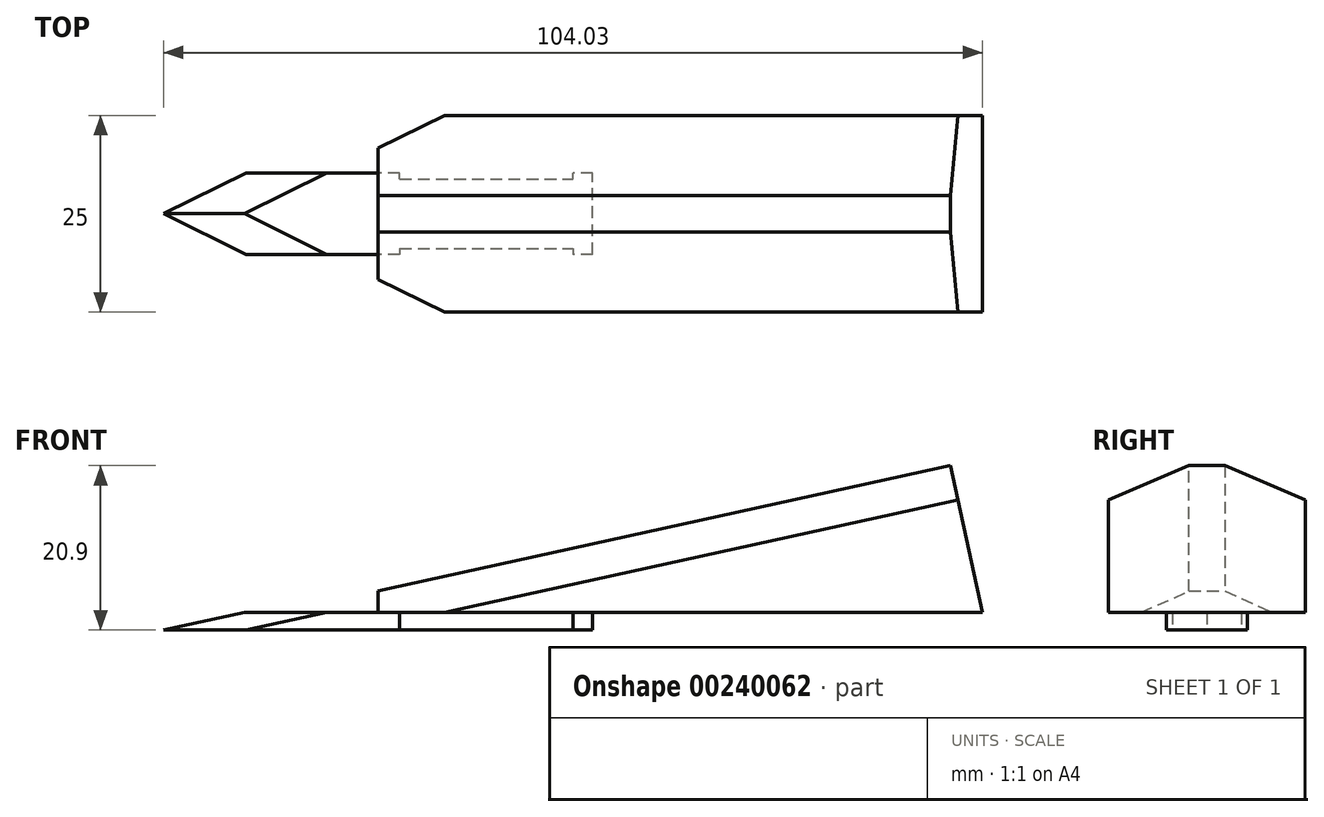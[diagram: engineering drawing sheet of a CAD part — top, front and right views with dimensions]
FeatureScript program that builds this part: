
annotation { "Feature Type Name" : "Feature", "Feature Type Description" : "" }
export const myFeature = defineFeature(function(context is Context, id is Id, definition is map)
    precondition{}
    {
        {
            var Q0;
            Q0=qCreatedBy(makeId("Top.planeOp"),FACE);
            var sketch = newSketch(context, id + "F0", { "sketchPlane" : qUnion([Q0])});
            skLineSegment(sketch, "E0.bottom", {"start": v(40.28, -18.54) * mm, "end": v(-40.28, -18.54) * mm});
            skLineSegment(sketch, "E0.top", {"start": v(40.28, 18.54) * mm, "end": v(-40.28, 18.54) * mm});
            skLineSegment(sketch, "E0.left", {"start": v(40.28, -18.54) * mm, "end": v(40.28, 18.54) * mm});
            skLineSegment(sketch, "E0.right", {"start": v(-40.28, -18.54) * mm, "end": v(-40.28, 18.54) * mm});
            skPoint(sketch, "E0.middle", {"position": v(0, 0) * mm});
            skLineSegment(sketch, "E1.bottom", {"start": v(27.25, -5.15) * mm, "end": v(-27.25, -5.15) * mm});
            skLineSegment(sketch, "E1.top", {"start": v(27.25, 5.15) * mm, "end": v(-27.25, 5.15) * mm});
            skLineSegment(sketch, "E1.left", {"start": v(27.25, -5.15) * mm, "end": v(27.25, 5.15) * mm});
            skLineSegment(sketch, "E1.right", {"start": v(-27.25, -5.15) * mm, "end": v(-27.25, 5.15) * mm});
            skLineSegment(sketch, "E2.bottom", {"start": v(2.75, -4.4) * mm, "end": v(24.75, -4.4) * mm});
            skLineSegment(sketch, "E2.top", {"start": v(2.75, -5.15) * mm, "end": v(24.75, -5.15) * mm});
            skLineSegment(sketch, "E2.left", {"start": v(2.75, -4.4) * mm, "end": v(2.75, -5.15) * mm});
            skLineSegment(sketch, "E2.right", {"start": v(24.75, -4.4) * mm, "end": v(24.75, -5.15) * mm});
            skLineSegment(sketch, "E3.MirrorCS", {"start": v(24.75, 4.4) * mm, "end": v(24.75, 5.15) * mm});
            skLineSegment(sketch, "E4.MirrorCS", {"start": v(2.75, 4.4) * mm, "end": v(24.75, 4.4) * mm});
            skLineSegment(sketch, "E5.MirrorCS", {"start": v(2.75, 4.4) * mm, "end": v(2.75, 5.15) * mm});
            skSolve(sketch);
        }
        {
            var Q0;
            {var subQ5=sQuery(id+"F0.wireOp",EDGE,"E1.left");Q0=makeQuery(id+"F0.imprint","IMPRINT",FACE,{"disambiguationData":[TD([[makeQuery(id+"F0.imprint","IMPRINT",EDGE,{"derivedFrom":subQ5}),1.0]])]});}
            extrude(context, id + "F1", {"entities" : qUnion([Q0]), "depth" : 2.25 * mm});
        }
        {
            var Q0;
            Q0=qCreatedBy(makeId("Front.planeOp"),FACE);
            var sketch = newSketch(context, id + "F2", { "sketchPlane" : qUnion([Q0])});
            skPoint(sketch, "E6.0", {"position": v(-27.25, 0) * mm});
            skLineSegment(sketch, "E7.0", {"start": v(2.75, 2.25) * mm, "end": v(-27.25, 2.25) * mm});
            skLineSegment(sketch, "E8.0", {"start": v(2.75, 0) * mm, "end": v(-27.25, 0) * mm});
            skLineSegment(sketch, "E9", {"start": v(-27.25, 0) * mm, "end": v(-17, 2.25) * mm});
            skLineSegment(sketch, "E10", {"start": v(-27.25, 0) * mm, "end": v(-6.52, 2.25) * mm, "construction": true});
            skLineSegment(sketch, "E11", {"start": v(-6.52, 2.25) * mm, "end": v(-16.78, 0) * mm});
            skLineSegment(sketch, "E12", {"start": v(-27.25, 0) * mm, "end": v(-27.25, 2.25) * mm});
            skPoint(sketch, "E13", {"position": v(-17, 2.25) * mm});
            skSolve(sketch);
        }
        {
            var Q0;
            {var subQ2=sQuery(id+"F2.wireOp",EDGE,"E9");Q0=makeQuery(id+"F2.imprint","IMPRINT",FACE,{"disambiguationData":[TD([[makeQuery(id+"F2.imprint","IMPRINT",EDGE,{"derivedFrom":subQ2}),1.0]])]});}
            extrude(context, id + "F3", {"entities" : qUnion([Q0]), "operationType" : NewBodyOperationType.REMOVE, "endBound" : BoundingType.SYMMETRIC, "oppositeDirection" : true, "depth" : 25 * mm});
        }
        {
            var Q0;
            {var subQ0=sQuery(id+"F0.wireOp",EDGE,"E1.bottom");Q0=makeQuery(id+"F1.opExtrude","SWEPT_FACE",FACE,{"disambiguationData":[OSD([subQ0]),TDD([makeQuery(id+"F0.imprint","IMPRINT",EDGE,{"disambiguationData":[TD([[makeQuery(id+"F0.imprint","INTERSECT",VERTEX,{"derivedFrom":[subQ0,sQuery(id+"F0.wireOp",EDGE,"E1.right")]}),1.0]])],"derivedFrom":subQ0})])]});}
            var sketch = newSketch(context, id + "F4", { "sketchPlane" : qUnion([Q0])});
            skLineSegment(sketch, "E14.0", {"start": v(-6.52, 2.25) * mm, "end": v(-16.78, 0) * mm});
            skLineSegment(sketch, "E15.0", {"start": v(2.75, 0) * mm, "end": v(-27.25, 0) * mm});
            skLineSegment(sketch, "E16.0", {"start": v(2.75, 2.25) * mm, "end": v(-27.25, 2.25) * mm});
            skPoint(sketch, "E17", {"position": v(-6.52, 2.25) * mm});
            skPoint(sketch, "E18", {"position": v(-16.78, 0) * mm});
            skSolve(sketch);
        }
        {
            var Q0;
            Q0=sQuery(id+"F2.wireOp",VERTEX,"E6.0");
            var Q1;
            Q1=sQuery(id+"F2.wireOp",VERTEX,"E13");
            var Q2;
            Q2=sQuery(id+"F4.wireOp",VERTEX,"E17");
            cPlane(context, id + "F5", {"entities" : qUnion([Q0, Q1, Q2]), "cplaneType" : CPlaneType.THREE_POINT, "offset" : 25 * mm, "width" : 150 * mm, "height" : 150 * mm});
        }
        {
            var Q0;
            Q0=qCreatedBy(id+"F5.planeOp",FACE);
            var sketch = newSketch(context, id + "F6", { "sketchPlane" : qUnion([Q0])});
            skPoint(sketch, "E19.0", {"position": v(-26.72, 0) * mm});
            skPoint(sketch, "E20.0", {"position": v(-16.26, 0.92) * mm});
            skPoint(sketch, "E21.0", {"position": v(-5.58, -3.79) * mm});
            skPoint(sketch, "E22.0", {"position": v(-16.04, -4.7) * mm});
            skLineSegment(sketch, "E23", {"start": v(-26.72, 0) * mm, "end": v(-16.26, 0.92) * mm});
            skLineSegment(sketch, "E24", {"start": v(-5.58, -3.79) * mm, "end": v(-16.26, 0.92) * mm});
            skLineSegment(sketch, "E25", {"start": v(-16.04, -4.7) * mm, "end": v(-26.72, 0) * mm});
            skLineSegment(sketch, "E26", {"start": v(-16.04, -4.7) * mm, "end": v(-5.58, -3.79) * mm});
            skLineSegment(sketch, "E27", {"start": v(-16.26, 0.92) * mm, "end": v(-27.12, 5.7) * mm});
            skLineSegment(sketch, "E28", {"start": v(-26.72, 0) * mm, "end": v(-37.58, 4.78) * mm});
            skLineSegment(sketch, "E29", {"start": v(-27.12, 5.7) * mm, "end": v(-37.58, 4.78) * mm});
            skLineSegment(sketch, "E30", {"start": v(-16.04, -4.7) * mm, "end": v(-43.24, -7.09) * mm});
            skLineSegment(sketch, "E31", {"start": v(-43.24, -7.09) * mm, "end": v(-37.58, 4.78) * mm});
            skSolve(sketch);
        }
        {
            var Q0;
            Q0=makeQuery(id+"F6.imprint","IMPRINT",FACE,{"disambiguationData":[TD([[makeQuery(id+"F6.imprint","IMPRINT",EDGE,{"derivedFrom":sQuery(id+"F6.wireOp",EDGE,"E23")}),-1.0]])]});
            var Q1;
            Q1=makeQuery(id+"F6.imprint","IMPRINT",FACE,{"disambiguationData":[TD([[makeQuery(id+"F6.imprint","IMPRINT",EDGE,{"derivedFrom":sQuery(id+"F6.wireOp",EDGE,"E23")}),1.0]])]});
            var Q2;
            Q2=makeQuery(id+"F6.imprint","IMPRINT",FACE,{"disambiguationData":[TD([[makeQuery(id+"F6.imprint","IMPRINT",EDGE,{"derivedFrom":sQuery(id+"F6.wireOp",EDGE,"E25")}),1.0]])]});
            extrude(context, id + "F7", {"entities" : qUnion([Q0, Q1, Q2]), "depth" : 25 * mm});
        }
        {
            var Q0;
            Q0=makeQuery(id+"F7.opExtrude","SWEPT_BODY",BODY,{"disambiguationData":[OSD([sQuery(id+"F6.wireOp",EDGE,"E24"),sQuery(id+"F6.wireOp",EDGE,"E26"),sQuery(id+"F6.wireOp",EDGE,"E27"),sQuery(id+"F6.wireOp",EDGE,"E29"),sQuery(id+"F6.wireOp",EDGE,"E30"),sQuery(id+"F6.wireOp",EDGE,"E31")])]});
            var Q1;
            Q1=qCreatedBy(makeId("Front.planeOp"),FACE);
            mirror(context, id + "F8", {"entities" : qUnion([Q0]), "mirrorPlane" : qUnion([Q1])});
        }
        {
            var Q0;
            Q0=makeQuery(id+"F7.opExtrude","SWEPT_BODY",BODY,{"disambiguationData":[OSD([sQuery(id+"F6.wireOp",EDGE,"E24"),sQuery(id+"F6.wireOp",EDGE,"E26"),sQuery(id+"F6.wireOp",EDGE,"E27"),sQuery(id+"F6.wireOp",EDGE,"E29"),sQuery(id+"F6.wireOp",EDGE,"E30"),sQuery(id+"F6.wireOp",EDGE,"E31")])]});
            var Q1;
            Q1=makeQuery(id+"F8.opPattern","COPY",BODY,{"derivedFrom":makeQuery(id+"F7.opExtrude","SWEPT_BODY",BODY,{"disambiguationData":[OSD([sQuery(id+"F6.wireOp",EDGE,"E24"),sQuery(id+"F6.wireOp",EDGE,"E26"),sQuery(id+"F6.wireOp",EDGE,"E27"),sQuery(id+"F6.wireOp",EDGE,"E29"),sQuery(id+"F6.wireOp",EDGE,"E30"),sQuery(id+"F6.wireOp",EDGE,"E31")])]}),"instanceName":"1"});
            var Q2;
            Q2=makeQuery(id+"F1.opExtrude","SWEPT_BODY",BODY,{"disambiguationData":[OSD([sQuery(id+"F0.wireOp",EDGE,"E1.bottom"),sQuery(id+"F0.wireOp",EDGE,"E1.top"),sQuery(id+"F0.wireOp",EDGE,"E1.left"),sQuery(id+"F0.wireOp",EDGE,"E1.right"),sQuery(id+"F0.wireOp",EDGE,"E2.bottom"),sQuery(id+"F0.wireOp",EDGE,"E2.left"),sQuery(id+"F0.wireOp",EDGE,"E2.right"),sQuery(id+"F0.wireOp",EDGE,"E3.MirrorCS"),sQuery(id+"F0.wireOp",EDGE,"E4.MirrorCS"),sQuery(id+"F0.wireOp",EDGE,"E5.MirrorCS")])]});
            booleanBodies(context, id + "F9", {"operationType" : BooleanOperationType.SUBTRACTION, "tools" : qUnion([Q0, Q1]), "targets" : qUnion([Q2])});
        }
        {
            var Q0;
            Q0=qCreatedBy(makeId("Front.planeOp"),FACE);
            var sketch = newSketch(context, id + "F10", { "sketchPlane" : qUnion([Q0])});
            skLineSegment(sketch, "E32.0", {"start": v(-17, 2.25) * mm, "end": v(-27.25, 0) * mm, "construction": true});
            skLineSegment(sketch, "E33", {"start": v(-17, 2.25) * mm, "end": v(80.68, 23.68) * mm, "construction": true});
            skLineSegment(sketch, "E34", {"start": v(0, 4.95) * mm, "end": v(72.69, 20.9) * mm});
            skLineSegment(sketch, "E35", {"start": v(72.69, 20.9) * mm, "end": v(76.78, 2.25) * mm});
            skPoint(sketch, "E36.orphan", {"position": v(0, 0) * mm});
            skLineSegment(sketch, "E37.0", {"start": v(2.75, 2.25) * mm, "end": v(-6.52, 2.25) * mm, "construction": true});
            skLineSegment(sketch, "E38", {"start": v(0, 2.25) * mm, "end": v(76.78, 2.25) * mm});
            skLineSegment(sketch, "E39", {"start": v(0, 2.25) * mm, "end": v(0, 4.95) * mm});
            skSolve(sketch);
        }
        {
            var Q0;
            Q0=makeQuery(id+"F10.imprint","IMPRINT",FACE,{"disambiguationData":[TD([[makeQuery(id+"F10.imprint","IMPRINT",EDGE,{"derivedFrom":sQuery(id+"F10.wireOp",EDGE,"E34")}),-1.0]])]});
            extrude(context, id + "F11", {"entities" : qUnion([Q0]), "endBound" : BoundingType.SYMMETRIC, "depth" : 25 * mm});
        }
        {
            var Q0;
            Q0=makeQuery(id+"F9.opBoolean","COPY",FACE,{"derivedFrom":makeQuery(id+"F7.opExtrude","CAP_FACE",FACE,{"disambiguationData":[OSD([sQuery(id+"F6.wireOp",EDGE,"E24"),sQuery(id+"F6.wireOp",EDGE,"E26"),sQuery(id+"F6.wireOp",EDGE,"E27"),sQuery(id+"F6.wireOp",EDGE,"E29"),sQuery(id+"F6.wireOp",EDGE,"E30"),sQuery(id+"F6.wireOp",EDGE,"E31")])],"isStart":true})});
            var sketch = newSketch(context, id + "F12", { "sketchPlane" : qUnion([Q0])});
            skLineSegment(sketch, "E40.0", {"start": v(-16.26, 0.92) * mm, "end": v(-26.72, 0) * mm});
            skLineSegment(sketch, "E41.0", {"start": v(-16.04, -4.7) * mm, "end": v(-5.58, -3.79) * mm});
            skLineSegment(sketch, "E42", {"start": v(-33.97, 3.2) * mm, "end": v(83.75, -48.65) * mm});
            skLineSegment(sketch, "E43", {"start": v(-33.97, 3.2) * mm, "end": v(-14.31, 47.83) * mm});
            skLineSegment(sketch, "E44", {"start": v(-14.31, 47.83) * mm, "end": v(103.41, -4.01) * mm});
            skLineSegment(sketch, "E45", {"start": v(103.41, -4.01) * mm, "end": v(83.75, -48.65) * mm});
            skSolve(sketch);
        }
        {
            var Q0;
            {var subQ3=sQuery(id+"F12.wireOp",EDGE,"E40.0");Q0=makeQuery(id+"F12.imprint","IMPRINT",FACE,{"disambiguationData":[TD([[makeQuery(id+"F12.imprint","IMPRINT",EDGE,{"derivedFrom":subQ3}),-1.0]])]});}
            extrude(context, id + "F13", {"entities" : qUnion([Q0]), "depth" : 25 * mm});
        }
        {
            var Q0;
            Q0=makeQuery(id+"F13.opExtrude","SWEPT_BODY",BODY,{"disambiguationData":[OSD([sQuery(id+"F6.wireOp",EDGE,"E24"),sQuery(id+"F6.wireOp",EDGE,"E27"),sQuery(id+"F12.wireOp",EDGE,"E40.0"),sQuery(id+"F12.wireOp",EDGE,"E41.0"),sQuery(id+"F12.wireOp",EDGE,"E42"),sQuery(id+"F12.wireOp",EDGE,"E43"),sQuery(id+"F12.wireOp",EDGE,"E44"),sQuery(id+"F12.wireOp",EDGE,"E45")])]});
            var Q1;
            Q1=qCreatedBy(makeId("Front.planeOp"),FACE);
            mirror(context, id + "F14", {"entities" : qUnion([Q0]), "mirrorPlane" : qUnion([Q1])});
        }
        {
            var Q0;
            Q0=makeQuery(id+"F14.opPattern","COPY",BODY,{"derivedFrom":makeQuery(id+"F13.opExtrude","SWEPT_BODY",BODY,{"disambiguationData":[OSD([sQuery(id+"F6.wireOp",EDGE,"E24"),sQuery(id+"F6.wireOp",EDGE,"E27"),sQuery(id+"F12.wireOp",EDGE,"E40.0"),sQuery(id+"F12.wireOp",EDGE,"E41.0"),sQuery(id+"F12.wireOp",EDGE,"E42"),sQuery(id+"F12.wireOp",EDGE,"E43"),sQuery(id+"F12.wireOp",EDGE,"E44"),sQuery(id+"F12.wireOp",EDGE,"E45")])]}),"instanceName":"1"});
            var Q1;
            Q1=makeQuery(id+"F13.opExtrude","SWEPT_BODY",BODY,{"disambiguationData":[OSD([sQuery(id+"F6.wireOp",EDGE,"E24"),sQuery(id+"F6.wireOp",EDGE,"E27"),sQuery(id+"F12.wireOp",EDGE,"E40.0"),sQuery(id+"F12.wireOp",EDGE,"E41.0"),sQuery(id+"F12.wireOp",EDGE,"E42"),sQuery(id+"F12.wireOp",EDGE,"E43"),sQuery(id+"F12.wireOp",EDGE,"E44"),sQuery(id+"F12.wireOp",EDGE,"E45")])]});
            var Q2;
            Q2=makeQuery(id+"F11.opExtrude","SWEPT_BODY",BODY,{"disambiguationData":[OSD([sQuery(id+"F10.wireOp",EDGE,"E34"),sQuery(id+"F10.wireOp",EDGE,"E35"),sQuery(id+"F10.wireOp",EDGE,"E38"),sQuery(id+"F10.wireOp",EDGE,"E39")])]});
            booleanBodies(context, id + "F15", {"operationType" : BooleanOperationType.SUBTRACTION, "tools" : qUnion([Q0, Q1]), "targets" : qUnion([Q2])});
        }
    });
